# Revit family: Calor Dry wall based
name_source: partatom
category: Mechanical Equipment
units: mm (PartAtom-declared; Revit-internal decimal feet)

## family parameters
Always vertical = Yes
Cut with Voids When Loaded = No
Host = Wall
OmniClass Number = 23.75.00.00
OmniClass Title = Climate Control (HVAC)
Part Type = Normal
Room Calculation Point = No
Round Connector Dimension = Use Diameter
Shared = No

## types (3) — shared parameters
Manufacturer = Masterwatt B.V.
URL = http://masterwatt.nl
Voltage = 230 V
zero-valued in all types: Default Elevation

## per-type parameters (varying)
| type | Art. No. | Product type | Watt |
| Calor Dry 350 | 300 120 350 | Calor Dry : Calor Dry 350 | 350 VA |
| Calor Dry 500 | 300 120 500 | Calor Dry : Calor Dry 500 | 500 VA |
| Calor Dry 750 | 300 120 750 | Calor Dry : Calor Dry 750 | 750 VA |

note: column(s) folded — value = type name in every type: Model

## geometry (parser evidence)
native form markers: Sweep x12
no freeform markers — native parametric forms only
